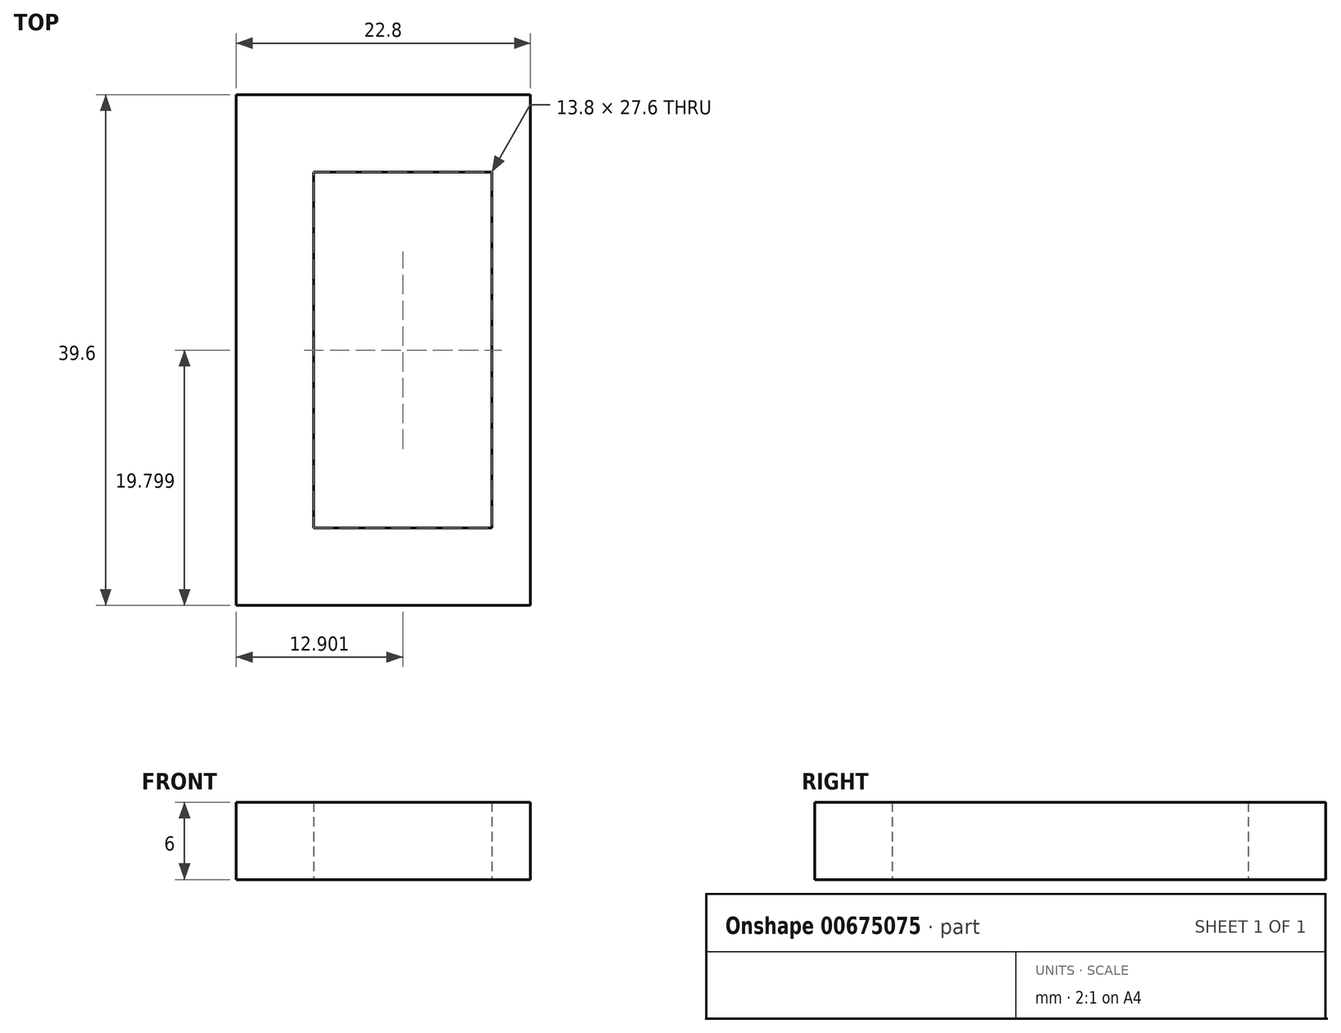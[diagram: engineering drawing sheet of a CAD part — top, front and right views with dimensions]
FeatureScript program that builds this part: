
annotation { "Feature Type Name" : "Feature", "Feature Type Description" : "" }
export const myFeature = defineFeature(function(context is Context, id is Id, definition is map)
    precondition{}
    {
        {
            var Q0;
            Q0=qCreatedBy(makeId("Top.planeOp"),FACE);
            var sketch = newSketch(context, id + "F0", { "sketchPlane" : qUnion([Q0])});
            skLineSegment(sketch, "E0.bottom", {"start": v(-117.72, 61.6) * mm, "end": v(-131.52, 61.6) * mm});
            skLineSegment(sketch, "E0.top", {"start": v(-117.72, 89.2) * mm, "end": v(-131.52, 89.2) * mm});
            skLineSegment(sketch, "E0.left", {"start": v(-117.72, 61.6) * mm, "end": v(-117.72, 89.2) * mm});
            skLineSegment(sketch, "E0.right", {"start": v(-131.52, 61.6) * mm, "end": v(-131.52, 89.2) * mm});
            skLineSegment(sketch, "E1.bottom", {"start": v(-114.72, 95.2) * mm, "end": v(-137.52, 95.2) * mm});
            skLineSegment(sketch, "E1.top", {"start": v(-114.72, 55.6) * mm, "end": v(-137.52, 55.6) * mm});
            skLineSegment(sketch, "E1.left", {"start": v(-114.72, 95.2) * mm, "end": v(-114.72, 55.6) * mm});
            skLineSegment(sketch, "E1.right", {"start": v(-137.52, 95.2) * mm, "end": v(-137.52, 55.6) * mm});
            skSolve(sketch);
        }
        {
            var Q0;
            Q0=makeQuery(id+"F0.imprint","IMPRINT",FACE,{"disambiguationData":[TD([[makeQuery(id+"F0.imprint","IMPRINT",EDGE,{"derivedFrom":sQuery(id+"F0.wireOp",EDGE,"E0.bottom")}),1.0]])]});
            extrude(context, id + "F1", {"entities" : qUnion([Q0]), "depth" : 6 * mm, "offsetDistance" : 25.4 * mm});
        }
    });
